# Revit family: БА150_RV17_LOD400 (05.11.23)
name_source: partatom
category: Электрооборудование
revit_build: Autodesk Revit 2017 (Build: 20170118_1100(x64)
units: mm (PartAtom-declared; Revit-internal decimal feet)

## family parameters
Всегда вертикально = Да
Конфигурация панели = Два столбца, слева направо
На основе рабочей плоскости = Нет
Общий = Нет
При загрузке вырезать с полостями = Нет
Размер круглого соединителя = Использовать диаметр
Тип детали = Щит
Точка расчета площади = Нет

## types (1)
- БА150
    ADSK_URL страницы изделия = https://stilsoft.ru
    ADSK_Единица измерения = шт.
    ADSK_Завод-изготовитель = ООО «Основа Безопасности»
    ADSK_Количество = 1
    ADSK_Марка = СТВФ.426471.554
    ADSK_Масса = 26.5
    ADSK_Наименование = Аудиоусилитель БА150
    ADSK_Размер_Высота = 500 мм
    ADSK_Размер_Глубина = 170 мм
    ADSK_Размер_Длина = 400 мм
    d_короба = 20 мм
    АКБ = Нет
    АКБ_2 = Нет
    Возможность объединения в единый комплекс по сети Ethernet = да
    Грозозащита на выходах линий оповещения = да
    Диапазон воспроизводимых частот речевого тракта, кГц = от 0,3 до 3,4
    Диапазон рабочих температур = от -50º до +55º
    Емкость / Напряжение АКБ, А*ч / В = 12 / 12
    Звуковое сопровождение трансляции видеоконтента на терминальных комплексах = да
    Интерфейс связи = 10BaseT/100 BaseTХ Ethernet (RJ-45)
    Количество АКБ, шт. = 2
    Количество линий оповещения, шт = 2
    Коэффициент нелинейных искажений на частоте 1000 Гц, не более, % = 5
    Коэффициенте гармоник, не более = 0.02
    Материал корпуса = нержавеющая сталь
    Мощность = 75
    Напряжение = 220
    Настройки уровня громкости сигнала для повседневного режима работы и для режима возникновения угрозы = да
    Номинальная / максимальная мощность на один канал, не менее, Вт = 75 / 100
    Номинальное выходное напряжение постоянного тока, В = 24
    Переключения АКБ-сеть 220В и обратно = онлайн
    Потребляемая изделием электрическая мощность (без учета системы обогрева), не более, Вт = 211
    Потребляемая системой обогрева электрическая мощность, не более, Вт = 200
    Разборчивость слов при передаче речевых сообщений, не менее, % = 93
    Размещение аккумуляторных батарей (АКБ) = в корпусе изделия
    Сохранение работоспособности при отключении энергоснабжения в дежурном режиме ожидания, не менее, час = 6
    Сохранение работоспособности при отключении энергоснабжения в режиме передачи сигналов и информации оповещения, не менее, час = 1
    Уровень звука речевых сообщений выше допустимого уровня звука постоянного шума, более чем на 15 дБ = да
    Уровень звука речевых сообщений на расстоянии 3м от  специального оконечного устройства оповещения населения = не менее 75
    Уровень звука речевых сообщенийв любой точке озвучивания пространства, дБ = не более 120
    дверь = Да
    диапазон частот при неравномерности АЧХ-3дБ, Гц = 20-20000
